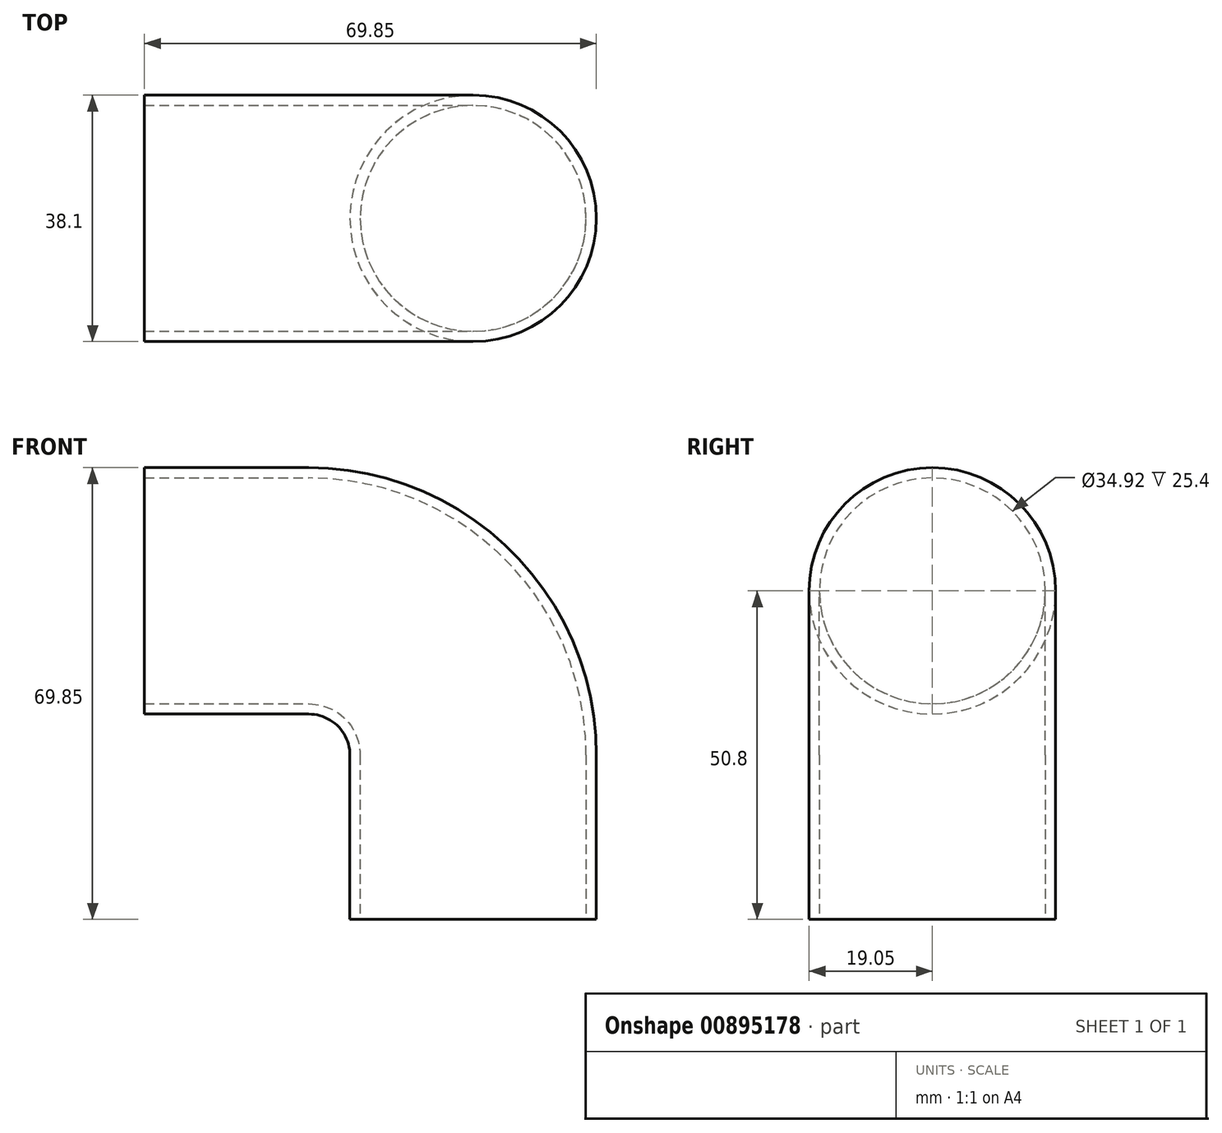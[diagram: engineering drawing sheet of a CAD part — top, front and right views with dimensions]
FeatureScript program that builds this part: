
annotation { "Feature Type Name" : "Feature", "Feature Type Description" : "" }
export const myFeature = defineFeature(function(context is Context, id is Id, definition is map)
    precondition{}
    {
        {
            var Q0;
            Q0=qCreatedBy(makeId("Front.planeOp"),FACE);
            var sketch = newSketch(context, id + "F0", { "sketchPlane" : qUnion([Q0])});
            skLineSegment(sketch, "E0", {"start": v(0, 0) * mm, "end": v(25.4, 0) * mm});
            skLineSegment(sketch, "E1", {"start": v(50.8, -25.4) * mm, "end": v(50.8, -50.8) * mm});
            skPoint(sketch, "E2.visualSharp", {"position": v(50.8, 0) * mm});
            skArc(sketch, "E2.filletArc", {"start": v(50.8, -25.4) * mm, "mid": v(43.36, -7.44) * mm, "end": v(25.4, 0) * mm});
            skSolve(sketch);
        }
        {
            var Q0;
            Q0=qCreatedBy(makeId("Right.planeOp"),FACE);
            var sketch = newSketch(context, id + "F1", { "sketchPlane" : qUnion([Q0])});
            skCircle(sketch, "E3", {"center": v(0, 0) * mm, "radius": 17.46 * mm});
            skCircle(sketch, "E4", {"center": v(0, 0) * mm, "radius": 19.05 * mm});
            skSolve(sketch);
        }
        {
            var Q0;
            Q0=makeQuery(id+"F1.imprint","IMPRINT",FACE,{"disambiguationData":[TD([[makeQuery(id+"F1.imprint","IMPRINT",EDGE,{"derivedFrom":sQuery(id+"F1.wireOp",EDGE,"E3")}),-1.0]])]});
            var Q1;
            Q1=sQuery(id+"F0.wireOp",EDGE,"E0");
            var Q2;
            Q2=sQuery(id+"F0.wireOp",EDGE,"E2.filletArc");
            var Q3;
            Q3=sQuery(id+"F0.wireOp",EDGE,"E1");
            sweep(context, id + "F2", {"profiles" : qUnion([Q0]), "path" : qUnion([Q1, Q2, Q3])});
        }
    });
